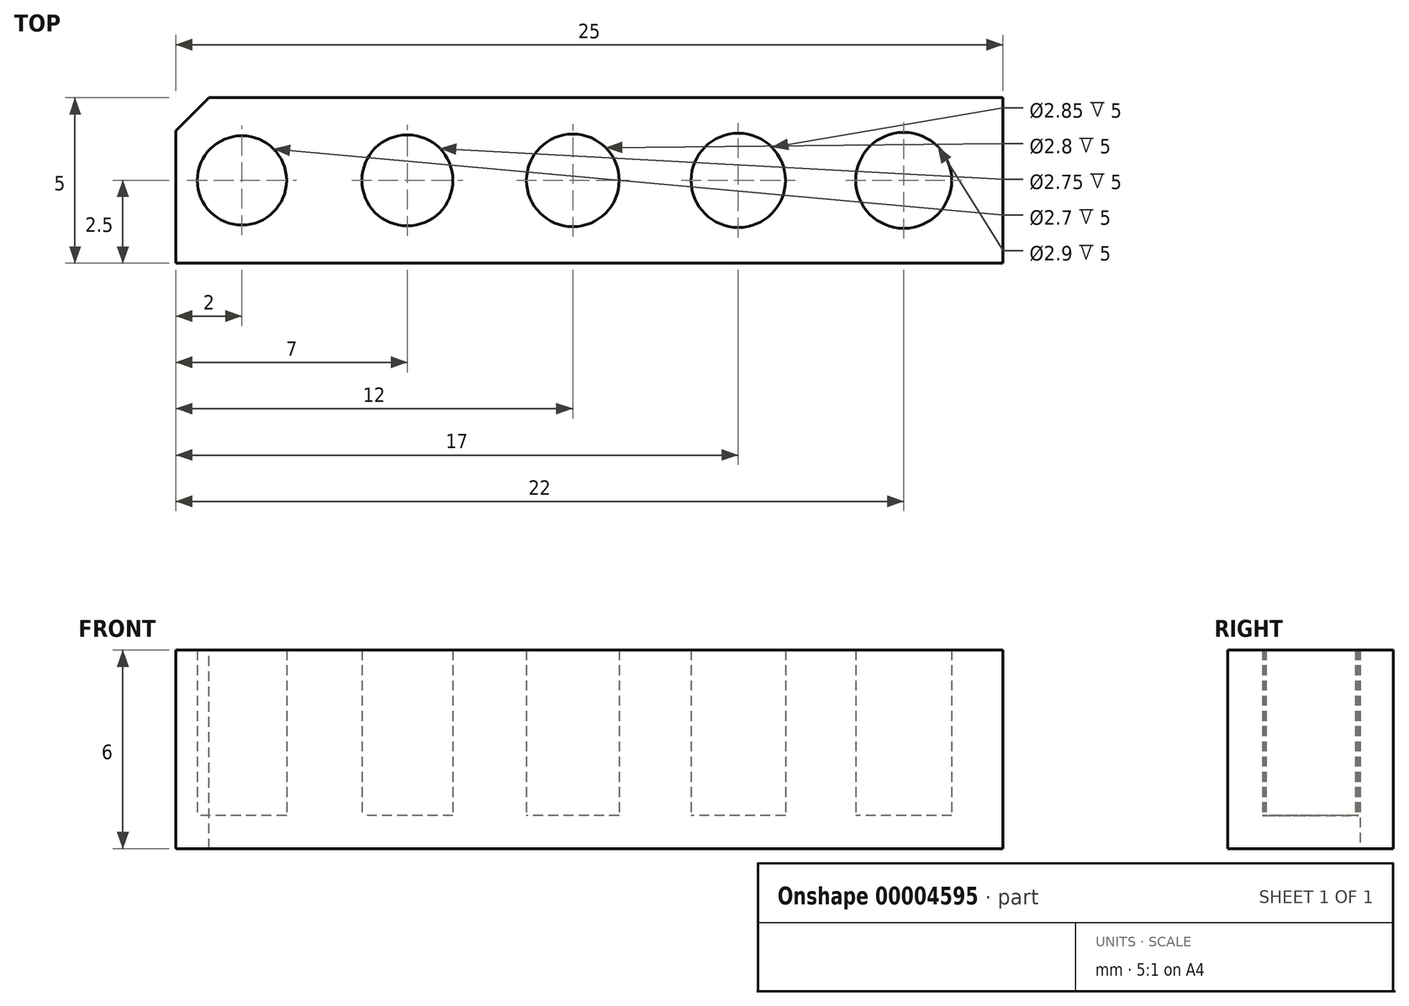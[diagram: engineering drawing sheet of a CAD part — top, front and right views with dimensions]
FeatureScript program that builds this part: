
annotation { "Feature Type Name" : "Feature", "Feature Type Description" : "" }
export const myFeature = defineFeature(function(context is Context, id is Id, definition is map)
    precondition{}
    {
        {
            var Q0;
            Q0=qCreatedBy(makeId("Top.planeOp"),FACE);
            var sketch = newSketch(context, id + "F0", { "sketchPlane" : qUnion([Q0])});
            skLineSegment(sketch, "E0.bottom", {"start": v(0, 0) * mm, "end": v(25, 0) * mm});
            skLineSegment(sketch, "E0.top", {"start": v(0, 5) * mm, "end": v(25, 5) * mm});
            skLineSegment(sketch, "E0.left", {"start": v(0, 0) * mm, "end": v(0, 5) * mm});
            skLineSegment(sketch, "E0.right", {"start": v(25, 0) * mm, "end": v(25, 5) * mm});
            skPoint(sketch, "E1", {"position": v(2, 2.5) * mm});
            skLineSegment(sketch, "E2", {"start": v(0, 2.5) * mm, "end": v(25, 2.5) * mm, "construction": true});
            skPoint(sketch, "E3.1.0.0", {"position": v(7, 2.5) * mm});
            skPoint(sketch, "E3.2.0.0", {"position": v(12, 2.5) * mm});
            skPoint(sketch, "E3.3.0.0", {"position": v(17, 2.5) * mm});
            skPoint(sketch, "E3.4.0.0", {"position": v(22, 2.5) * mm});
            skLineSegment(sketch, "E3.direction1", {"start": v(2, 2.5) * mm, "end": v(7, 2.5) * mm, "construction": true});
            skCircle(sketch, "E4", {"center": v(2, 2.5) * mm, "radius": 1.35 * mm});
            skCircle(sketch, "E5", {"center": v(7, 2.5) * mm, "radius": 1.38 * mm});
            skCircle(sketch, "E6", {"center": v(12, 2.5) * mm, "radius": 1.4 * mm});
            skCircle(sketch, "E7", {"center": v(17, 2.5) * mm, "radius": 1.43 * mm});
            skCircle(sketch, "E8", {"center": v(22, 2.5) * mm, "radius": 1.45 * mm});
            skSolve(sketch);
        }
        {
            var Q0;
            Q0=makeQuery(id+"F0.imprint","IMPRINT",FACE,{"disambiguationData":[TD([[makeQuery(id+"F0.imprint","IMPRINT",EDGE,{"derivedFrom":sQuery(id+"F0.wireOp",EDGE,"E0.bottom")}),1.0]])]});
            var Q1;
            Q1=makeQuery(id+"F0.imprint","IMPRINT",FACE,{"disambiguationData":[TD([[makeQuery(id+"F0.imprint","IMPRINT",EDGE,{"derivedFrom":sQuery(id+"F0.wireOp",EDGE,"E4")}),1.0]])]});
            var Q2;
            Q2=makeQuery(id+"F0.imprint","IMPRINT",FACE,{"disambiguationData":[TD([[makeQuery(id+"F0.imprint","IMPRINT",EDGE,{"derivedFrom":sQuery(id+"F0.wireOp",EDGE,"E5")}),1.0]])]});
            var Q3;
            Q3=makeQuery(id+"F0.imprint","IMPRINT",FACE,{"disambiguationData":[TD([[makeQuery(id+"F0.imprint","IMPRINT",EDGE,{"derivedFrom":sQuery(id+"F0.wireOp",EDGE,"E6")}),1.0]])]});
            var Q4;
            Q4=makeQuery(id+"F0.imprint","IMPRINT",FACE,{"disambiguationData":[TD([[makeQuery(id+"F0.imprint","IMPRINT",EDGE,{"derivedFrom":sQuery(id+"F0.wireOp",EDGE,"E7")}),1.0]])]});
            var Q5;
            Q5=makeQuery(id+"F0.imprint","IMPRINT",FACE,{"disambiguationData":[TD([[makeQuery(id+"F0.imprint","IMPRINT",EDGE,{"derivedFrom":sQuery(id+"F0.wireOp",EDGE,"E8")}),1.0]])]});
            extrude(context, id + "F1", {"entities" : qUnion([Q0, Q1, Q2, Q3, Q4, Q5]), "oppositeDirection" : true, "depth" : 1 * mm});
        }
        {
            var Q0;
            Q0=makeQuery(id+"F0.imprint","IMPRINT",FACE,{"disambiguationData":[TD([[makeQuery(id+"F0.imprint","IMPRINT",EDGE,{"derivedFrom":sQuery(id+"F0.wireOp",EDGE,"E0.bottom")}),1.0]])]});
            extrude(context, id + "F2", {"entities" : qUnion([Q0]), "operationType" : NewBodyOperationType.ADD, "depth" : 5 * mm});
        }
        {
            var Q0;
            {var subQ0=sQuery(id+"F0.wireOp",EDGE,"E0.top");var subQ1=sQuery(id+"F0.wireOp",EDGE,"E0.left");Q0=makeQuery(id+"F2.boolean.opBoolean","MERGE",EDGE,{"derivedFrom":[makeQuery(id+"F1.opExtrude","SWEPT_EDGE",EDGE,{"disambiguationData":[OSD([subQ0,subQ1])]}),makeQuery(id+"F2.opExtrude","SWEPT_EDGE",EDGE,{"disambiguationData":[OSD([subQ0,subQ1])]})]});}
            chamfer(context, id + "F3", {"entities" : qUnion([Q0]), "width" : 1 * mm, "tangentPropagation" : true});
        }
    });
